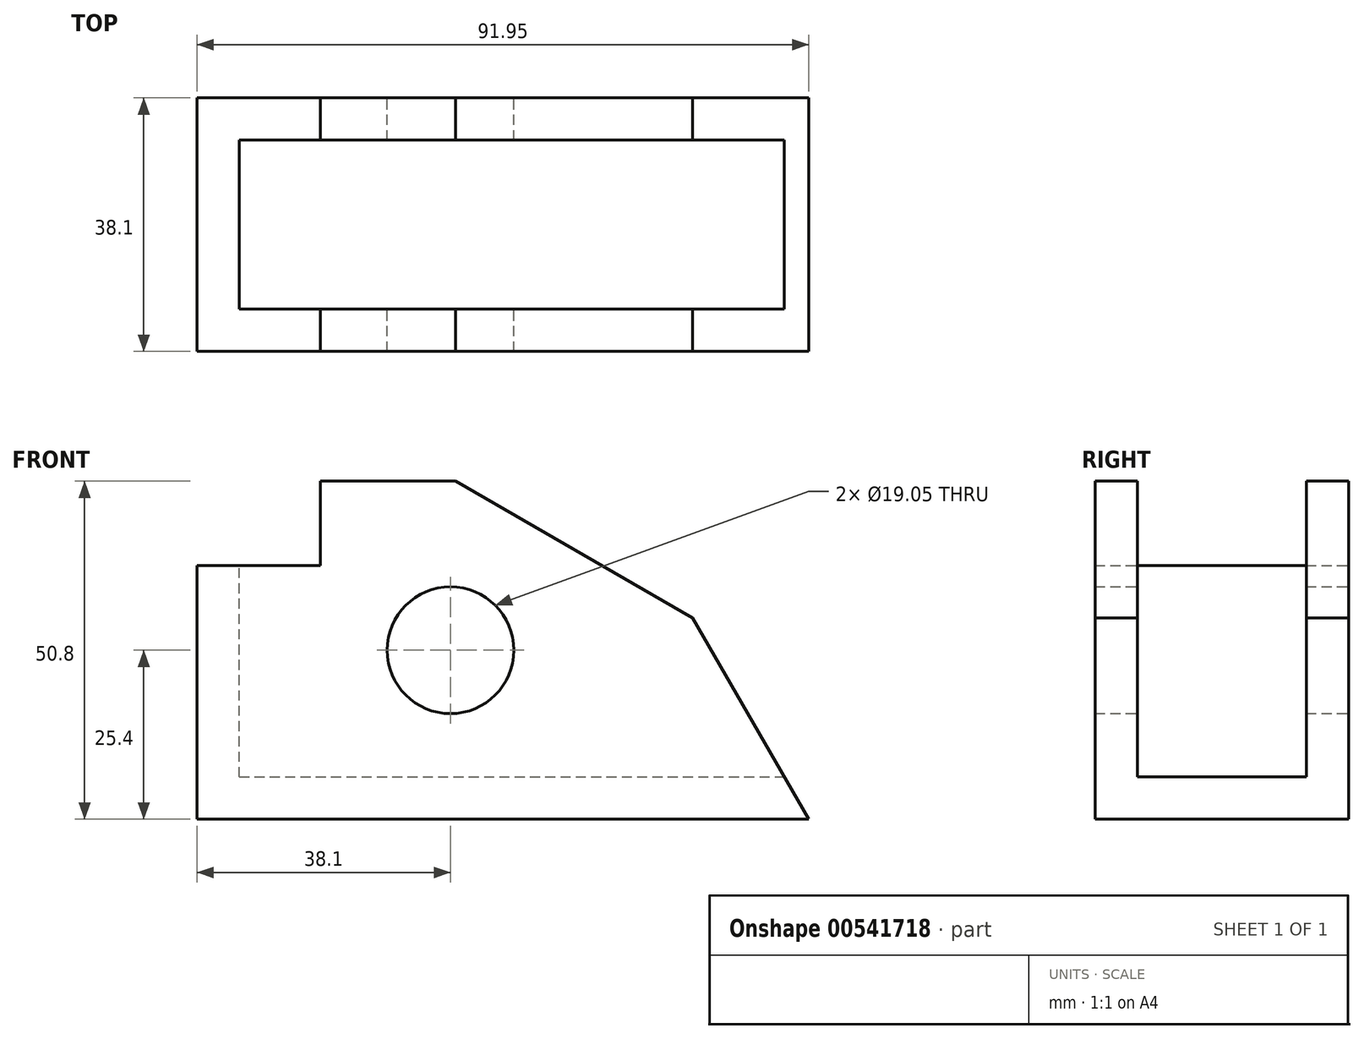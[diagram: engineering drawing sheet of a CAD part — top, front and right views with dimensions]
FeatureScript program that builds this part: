
annotation { "Feature Type Name" : "Feature", "Feature Type Description" : "" }
export const myFeature = defineFeature(function(context is Context, id is Id, definition is map)
    precondition{}
    {
        {
            var Q0;
            Q0=qCreatedBy(makeId("Front.planeOp"),FACE);
            var sketch = newSketch(context, id + "F0", { "sketchPlane" : qUnion([Q0])});
            skLineSegment(sketch, "E0", {"start": v(0, 0) * mm, "end": v(91.95, 0) * mm});
            skLineSegment(sketch, "E1", {"start": v(91.95, 0) * mm, "end": v(74.5, 30.23) * mm});
            skLineSegment(sketch, "E2", {"start": v(74.5, 30.23) * mm, "end": v(38.86, 50.8) * mm});
            skLineSegment(sketch, "E3", {"start": v(38.86, 50.8) * mm, "end": v(18.54, 50.8) * mm});
            skLineSegment(sketch, "E4", {"start": v(18.54, 50.8) * mm, "end": v(18.54, 38.1) * mm});
            skLineSegment(sketch, "E5", {"start": v(18.54, 38.1) * mm, "end": v(0, 38.1) * mm});
            skLineSegment(sketch, "E6", {"start": v(0, 38.1) * mm, "end": v(0, 0) * mm});
            skCircle(sketch, "E7", {"center": v(38.1, 25.4) * mm, "radius": 9.53 * mm});
            skSolve(sketch);
        }
        {
            var Q0;
            Q0=makeQuery(id+"F0.imprint","IMPRINT",FACE,{"disambiguationData":[TD([[makeQuery(id+"F0.imprint","IMPRINT",EDGE,{"derivedFrom":sQuery(id+"F0.wireOp",EDGE,"E0")}),1.0]])]});
            extrude(context, id + "F1", {"entities" : qUnion([Q0]), "depth" : 38.1 * mm, "offsetDistance" : 25.4 * mm});
        }
        {
            var Q0;
            Q0=makeQuery(id+"F1.opExtrude","SWEPT_FACE",FACE,{"disambiguationData":[OSD([sQuery(id+"F0.wireOp",EDGE,"E3")])]});
            var sketch = newSketch(context, id + "F2", { "sketchPlane" : qUnion([Q0])});
            skLineSegment(sketch, "E8.bottom", {"start": v(6.35, -31.75) * mm, "end": v(91.95, -31.75) * mm});
            skLineSegment(sketch, "E8.top", {"start": v(6.35, -6.35) * mm, "end": v(91.95, -6.35) * mm});
            skLineSegment(sketch, "E8.left", {"start": v(6.35, -31.75) * mm, "end": v(6.35, -6.35) * mm});
            skLineSegment(sketch, "E8.right", {"start": v(91.95, -31.75) * mm, "end": v(91.95, -6.35) * mm});
            skSolve(sketch);
        }
        {
            var Q0;
            {var subQ0=sQuery(id+"F2.wireOp",EDGE,"E8.left");Q0=makeQuery(id+"F2.imprint","IMPRINT",FACE,{"disambiguationData":[TD([[makeQuery(id+"F2.imprint","IMPRINT",EDGE,{"derivedFrom":subQ0}),-1.0]])]});}
            var Q1;
            {var subQ0=sQuery(id+"F2.wireOp",EDGE,"E8.bottom");var subQ1=sQuery(id+"F0.wireOp",EDGE,"E3");var subQ2=makeQuery(id+"F1.opExtrude","SWEPT_EDGE",EDGE,{"disambiguationData":[OSD([subQ1,sQuery(id+"F0.wireOp",EDGE,"E4")])]});var subQ3=makeQuery(id+"F2.imprint","INTERSECT",VERTEX,{"derivedFrom":[subQ2,subQ0]});Q1=makeQuery(id+"F2.imprint","IMPRINT",FACE,{"disambiguationData":[TD([[makeQuery(id+"F2.imprint","IMPRINT",EDGE,{"disambiguationData":[TD([[subQ3,-1.0]])],"derivedFrom":subQ0}),1.0]])]});}
            var Q2;
            {var subQ0=sQuery(id+"F2.wireOp",EDGE,"E8.right");Q2=makeQuery(id+"F2.imprint","IMPRINT",FACE,{"disambiguationData":[TD([[makeQuery(id+"F2.imprint","IMPRINT",EDGE,{"derivedFrom":subQ0}),1.0]])]});}
            extrude(context, id + "F3", {"entities" : qUnion([Q0, Q1, Q2]), "operationType" : NewBodyOperationType.REMOVE, "oppositeDirection" : true, "depth" : 44.45 * mm, "offsetDistance" : 25.4 * mm});
        }
    });
